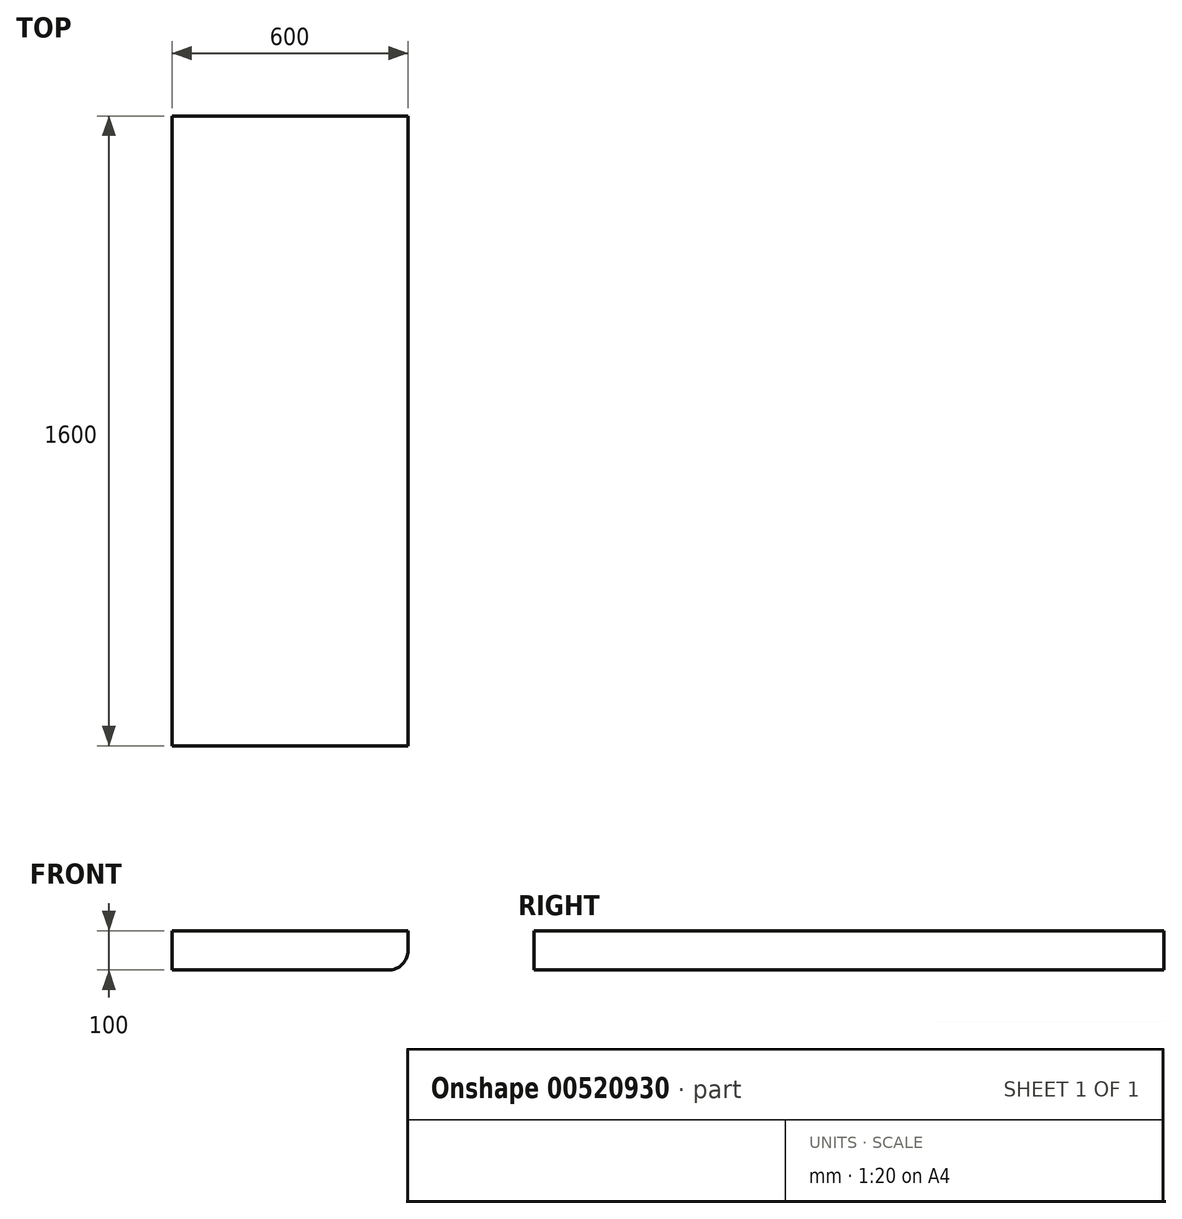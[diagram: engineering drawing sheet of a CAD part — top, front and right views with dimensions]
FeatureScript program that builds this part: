
annotation { "Feature Type Name" : "Feature", "Feature Type Description" : "" }
export const myFeature = defineFeature(function(context is Context, id is Id, definition is map)
    precondition{}
    {
        {
            var Q0;
            Q0=qCreatedBy(makeId("Top.planeOp"),FACE);
            var sketch = newSketch(context, id + "F0", { "sketchPlane" : qUnion([Q0])});
            skLineSegment(sketch, "E0.bottom", {"start": v(0, 800) * mm, "end": v(600, 800) * mm});
            skLineSegment(sketch, "E0.top", {"start": v(0, -800) * mm, "end": v(600, -800) * mm});
            skLineSegment(sketch, "E0.left", {"start": v(0, 800) * mm, "end": v(0, -800) * mm});
            skLineSegment(sketch, "E0.right", {"start": v(600, 800) * mm, "end": v(600, -800) * mm});
            skSolve(sketch);
        }
        {
            var Q0;
            Q0=makeQuery(id+"F0.imprint","IMPRINT",FACE,{"disambiguationData":[TD([[makeQuery(id+"F0.imprint","IMPRINT",EDGE,{"derivedFrom":sQuery(id+"F0.wireOp",EDGE,"E0.bottom")}),-1.0]])]});
            extrude(context, id + "F1", {"entities" : qUnion([Q0]), "depth" : 100 * mm, "offsetDistance" : 25 * mm});
        }
        {
            var Q0;
            Q0=makeQuery(id+"F1.opExtrude","CAP_EDGE",EDGE,{"disambiguationData":[OSD([sQuery(id+"F0.wireOp",EDGE,"E0.right")])],"isStart":true});
            fillet(context, id + "F2", {"entities" : qUnion([Q0]), "radius" : 50 * mm, "tangentPropagation" : true, "allowEdgeOverflow" : false});
        }
    });
